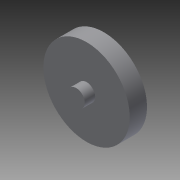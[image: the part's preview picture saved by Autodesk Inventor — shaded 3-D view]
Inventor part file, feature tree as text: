
AUTODESK INVENTOR PART (.ipt)
format: ipt  version: 2013 (Build 170138000, 138)  size: 83,456 bytes
history: native  units: mm
features: extrude x3, sketch x3, other x1
ambient origin geometry x8: Origin, YZ Plane, XZ Plane, XY Plane, X Axis, Y Axis, Z Axis, Center Point
feature tree (7):
  other  "ソリッド1"
  extrude  "押し出し1"  Depth=25.0mm
  extrude  "押し出し2"  Depth=5.0mm TaperAngle=0.0deg
  extrude  "押し出し3"  Depth=5.0mm
  sketch  "スケッチ1"
  sketch  "スケッチ2"
  sketch  "スケッチ3"
